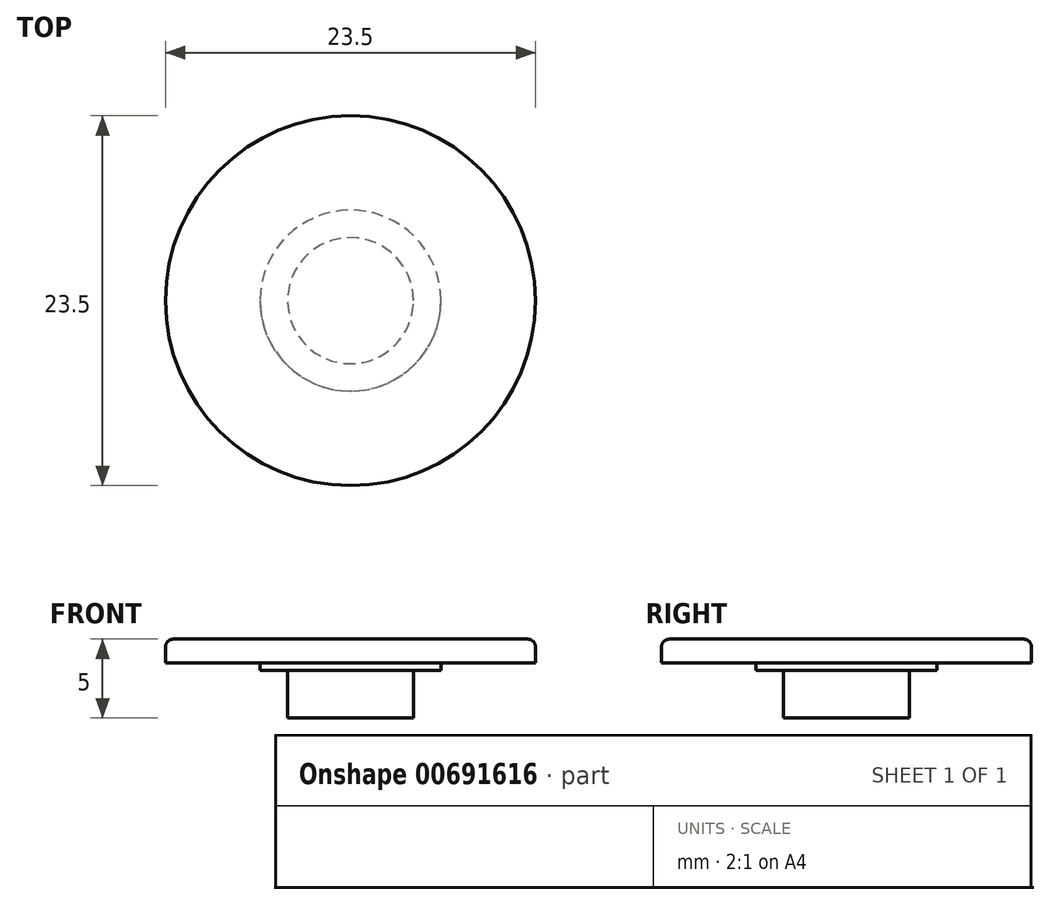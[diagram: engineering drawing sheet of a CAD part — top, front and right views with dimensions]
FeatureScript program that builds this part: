
annotation { "Feature Type Name" : "Feature", "Feature Type Description" : "" }
export const myFeature = defineFeature(function(context is Context, id is Id, definition is map)
    precondition{}
    {
        {
            var Q0;
            Q0=qCreatedBy(makeId("Top.planeOp"),FACE);
            var sketch = newSketch(context, id + "F0", { "sketchPlane" : qUnion([Q0])});
            skCircle(sketch, "E0", {"center": v(0, 0) * mm, "radius": 11.75 * mm});
            skSolve(sketch);
        }
        {
            var Q0;
            Q0=makeQuery(id+"F0.imprint","IMPRINT",FACE,{"disambiguationData":[TD([[makeQuery(id+"F0.imprint","IMPRINT",EDGE,{"derivedFrom":sQuery(id+"F0.wireOp",EDGE,"E0")}),1.0]])]});
            extrude(context, id + "F1", {"entities" : qUnion([Q0]), "oppositeDirection" : true, "depth" : 1.5 * mm, "offsetDistance" : 25 * mm});
        }
        {
            var Q0;
            Q0=makeQuery(id+"F1.opExtrude","CAP_EDGE",EDGE,{"disambiguationData":[OSD([sQuery(id+"F0.wireOp",EDGE,"E0")])],"isStart":true});
            fillet(context, id + "F2", {"entities" : qUnion([Q0]), "radius" : .5 * mm, "tangentPropagation" : true, "allowEdgeOverflow" : false});
        }
        {
            var Q0;
            Q0=makeQuery(id+"F1.opExtrude","CAP_FACE",FACE,{"disambiguationData":[OSD([sQuery(id+"F0.wireOp",EDGE,"E0")])],"isStart":false});
            var sketch = newSketch(context, id + "F3", { "sketchPlane" : qUnion([Q0])});
            skCircle(sketch, "E1", {"center": v(0, 0) * mm, "radius": 4 * mm});
            skSolve(sketch);
        }
        {
            var Q0;
            Q0=makeQuery(id+"F3.imprint","IMPRINT",FACE,{"disambiguationData":[TD([[makeQuery(id+"F3.imprint","IMPRINT",EDGE,{"derivedFrom":sQuery(id+"F3.wireOp",EDGE,"E1")}),1.0]])]});
            extrude(context, id + "F4", {"entities" : qUnion([Q0]), "operationType" : NewBodyOperationType.ADD, "depth" : 3.5 * mm, "offsetDistance" : 25 * mm});
        }
        {
            var Q0;
            Q0=makeQuery(id+"F1.opExtrude","CAP_FACE",FACE,{"disambiguationData":[OSD([sQuery(id+"F0.wireOp",EDGE,"E0")])],"isStart":false});
            var sketch = newSketch(context, id + "F5", { "sketchPlane" : qUnion([Q0])});
            skCircle(sketch, "E2", {"center": v(0, 0) * mm, "radius": 5.75 * mm});
            skSolve(sketch);
        }
        {
            var Q0;
            Q0=makeQuery(id+"F5.imprint","IMPRINT",FACE,{"disambiguationData":[TD([[makeQuery(id+"F5.imprint","IMPRINT",EDGE,{"derivedFrom":sQuery(id+"F5.wireOp",EDGE,"E2")}),1.0]])]});
            extrude(context, id + "F6", {"entities" : qUnion([Q0]), "operationType" : NewBodyOperationType.ADD, "depth" : .5 * mm, "offsetDistance" : 25 * mm});
        }
    });
